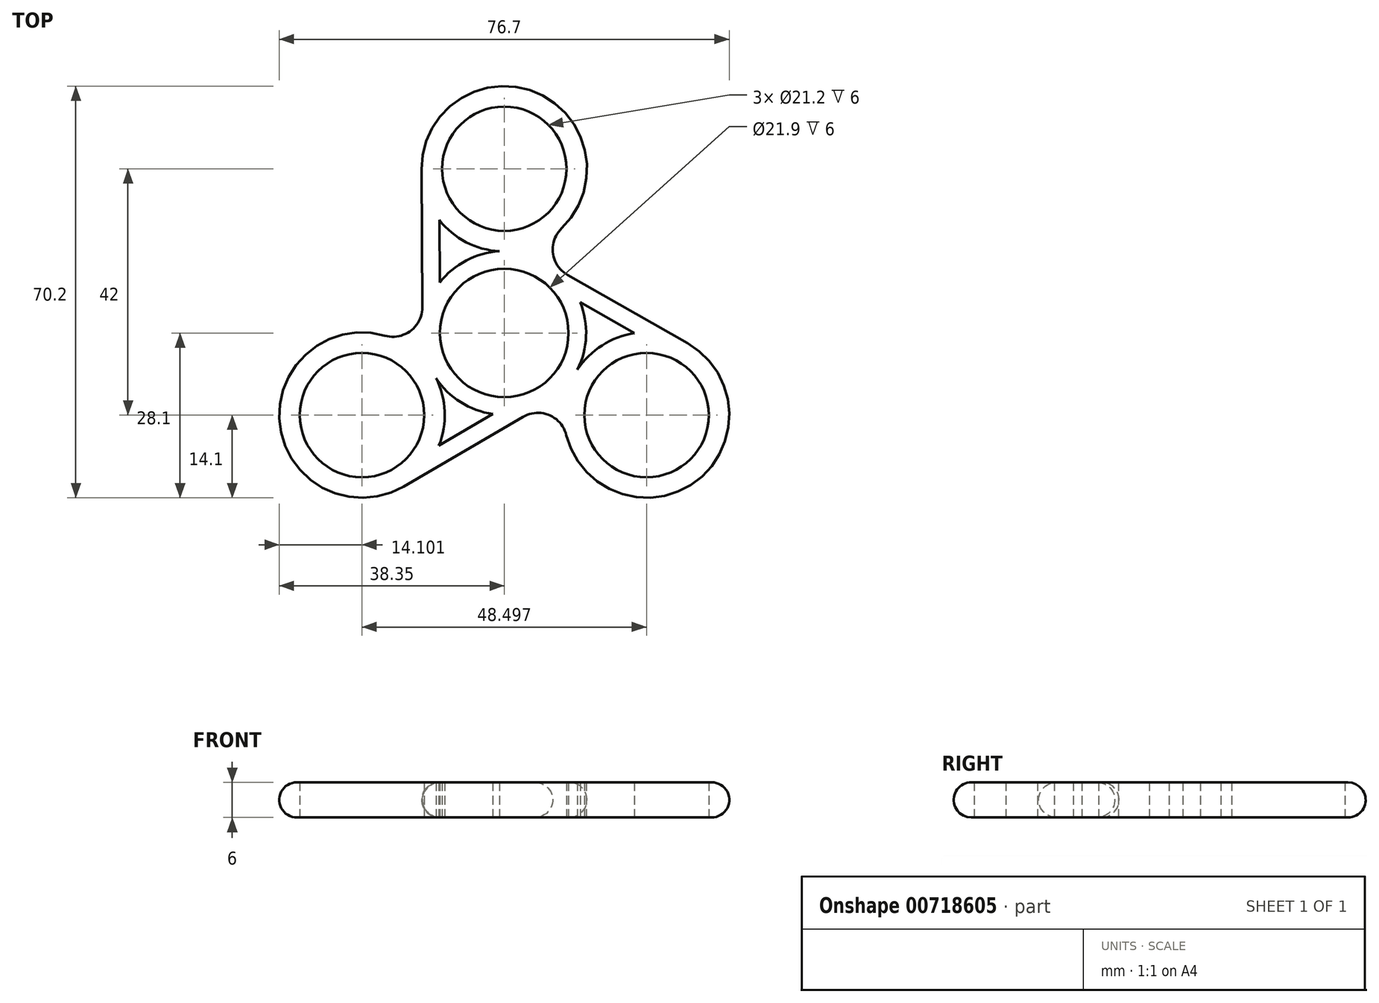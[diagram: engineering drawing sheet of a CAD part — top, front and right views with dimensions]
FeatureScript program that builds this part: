
annotation { "Feature Type Name" : "Feature", "Feature Type Description" : "" }
export const myFeature = defineFeature(function(context is Context, id is Id, definition is map)
    precondition{}
    {
        {
            var Q0;
            Q0=qCreatedBy(makeId("Top.planeOp"),FACE);
            var sketch = newSketch(context, id + "F0", { "sketchPlane" : qUnion([Q0])});
            skCircle(sketch, "E0", {"center": v(0, 0) * mm, "radius": 10.95 * mm});
            skCircle(sketch, "E1.cCircle", {"center": v(0, 0) * mm, "radius": 14 * mm, "construction": true});
            skLineSegment(sketch, "E1.0", {"start": v(0, 28) * mm, "end": v(24.25, -14) * mm, "construction": true});
            skLineSegment(sketch, "E1.1", {"start": v(24.25, -14) * mm, "end": v(-24.25, -14) * mm, "construction": true});
            skLineSegment(sketch, "E1.2", {"start": v(-24.25, -14) * mm, "end": v(0, 28) * mm, "construction": true});
            skPoint(sketch, "E1.0.midPoint", {"position": v(12.12, 7) * mm});
            skCircle(sketch, "E2", {"center": v(0, 28) * mm, "radius": 10.6 * mm});
            skCircle(sketch, "E3", {"center": v(24.25, -14) * mm, "radius": 10.6 * mm});
            skCircle(sketch, "E4", {"center": v(-24.25, -14) * mm, "radius": 10.6 * mm});
            skCircle(sketch, "E5.0", {"center": v(0, 0) * mm, "radius": 13.95 * mm});
            skCircle(sketch, "E6.0", {"center": v(0, 28) * mm, "radius": 14.1 * mm});
            skCircle(sketch, "E7.0", {"center": v(-24.25, -14) * mm, "radius": 14.1 * mm});
            skCircle(sketch, "E8.0", {"center": v(24.25, -14) * mm, "radius": 14.1 * mm});
            skLineSegment(sketch, "E9", {"start": v(-14.1, 27.92) * mm, "end": v(-13.95, -0.07) * mm});
            skLineSegment(sketch, "E10", {"start": v(7.04, -12.04) * mm, "end": v(-17.13, -26.17) * mm});
            skLineSegment(sketch, "E11", {"start": v(31.23, -1.75) * mm, "end": v(6.91, 12.12) * mm});
            skLineSegment(sketch, "E12.0", {"start": v(-11.1, 28.86) * mm, "end": v(-10.96, 0.91) * mm});
            skLineSegment(sketch, "E13.0", {"start": v(4.69, -9.94) * mm, "end": v(-19.44, -24.05) * mm});
            skLineSegment(sketch, "E14.0", {"start": v(30.54, -4.81) * mm, "end": v(6.27, 9.03) * mm});
            skSolve(sketch);
        }
        {
            var Q0;
            Q0=qSketchRegion(id+"F0",true);
            extrude(context, id + "F1", {"entities" : qUnion([Q0]), "depth" : 6 * mm, "offsetDistance" : 25 * mm});
        }
        {
            var Q0;
            {var subQ0=sQuery(id+"F0.wireOp",EDGE,"E8.0");var subQ1=sQuery(id+"F0.wireOp",EDGE,"E5.0");Q0=makeQuery(id+"F1.opExtrude","SWEPT_EDGE",EDGE,{"disambiguationData":[OSD([subQ1,subQ0]),TDD([makeQuery(id+"F0.imprint","INTERSECT",VERTEX,{"disambiguationData":[OD(0.0)],"derivedFrom":[subQ1,subQ0]})])]});}
            var Q1;
            {var subQ0=sQuery(id+"F0.wireOp",EDGE,"E6.0");var subQ1=sQuery(id+"F0.wireOp",EDGE,"E5.0");Q1=makeQuery(id+"F1.opExtrude","SWEPT_EDGE",EDGE,{"disambiguationData":[OSD([subQ1,subQ0]),TDD([makeQuery(id+"F0.imprint","INTERSECT",VERTEX,{"disambiguationData":[OD(0.0)],"derivedFrom":[subQ1,subQ0]})])]});}
            var Q2;
            {var subQ0=sQuery(id+"F0.wireOp",EDGE,"E7.0");var subQ1=sQuery(id+"F0.wireOp",EDGE,"E5.0");Q2=makeQuery(id+"F1.opExtrude","SWEPT_EDGE",EDGE,{"disambiguationData":[OSD([subQ1,subQ0]),TDD([makeQuery(id+"F0.imprint","INTERSECT",VERTEX,{"disambiguationData":[OD(0.0)],"derivedFrom":[subQ1,subQ0]})])]});}
            fillet(context, id + "F2", {"entities" : qUnion([Q0, Q1, Q2]), "radius" : 5 * mm, "tangentPropagation" : true, "allowEdgeOverflow" : false});
        }
        {
            var Q0;
            Q0=makeQuery(id+"F1.opExtrude","CAP_EDGE",EDGE,{"disambiguationData":[OSD([sQuery(id+"F0.wireOp",EDGE,"E10")])],"isStart":false});
            var Q1;
            Q1=makeQuery(id+"F1.opExtrude","CAP_EDGE",EDGE,{"disambiguationData":[OSD([sQuery(id+"F0.wireOp",EDGE,"E10")])],"isStart":true});
            fillet(context, id + "F3", {"entities" : qUnion([Q0, Q1]), "radius" : 3 * mm, "tangentPropagation" : true, "allowEdgeOverflow" : false});
        }
    });
